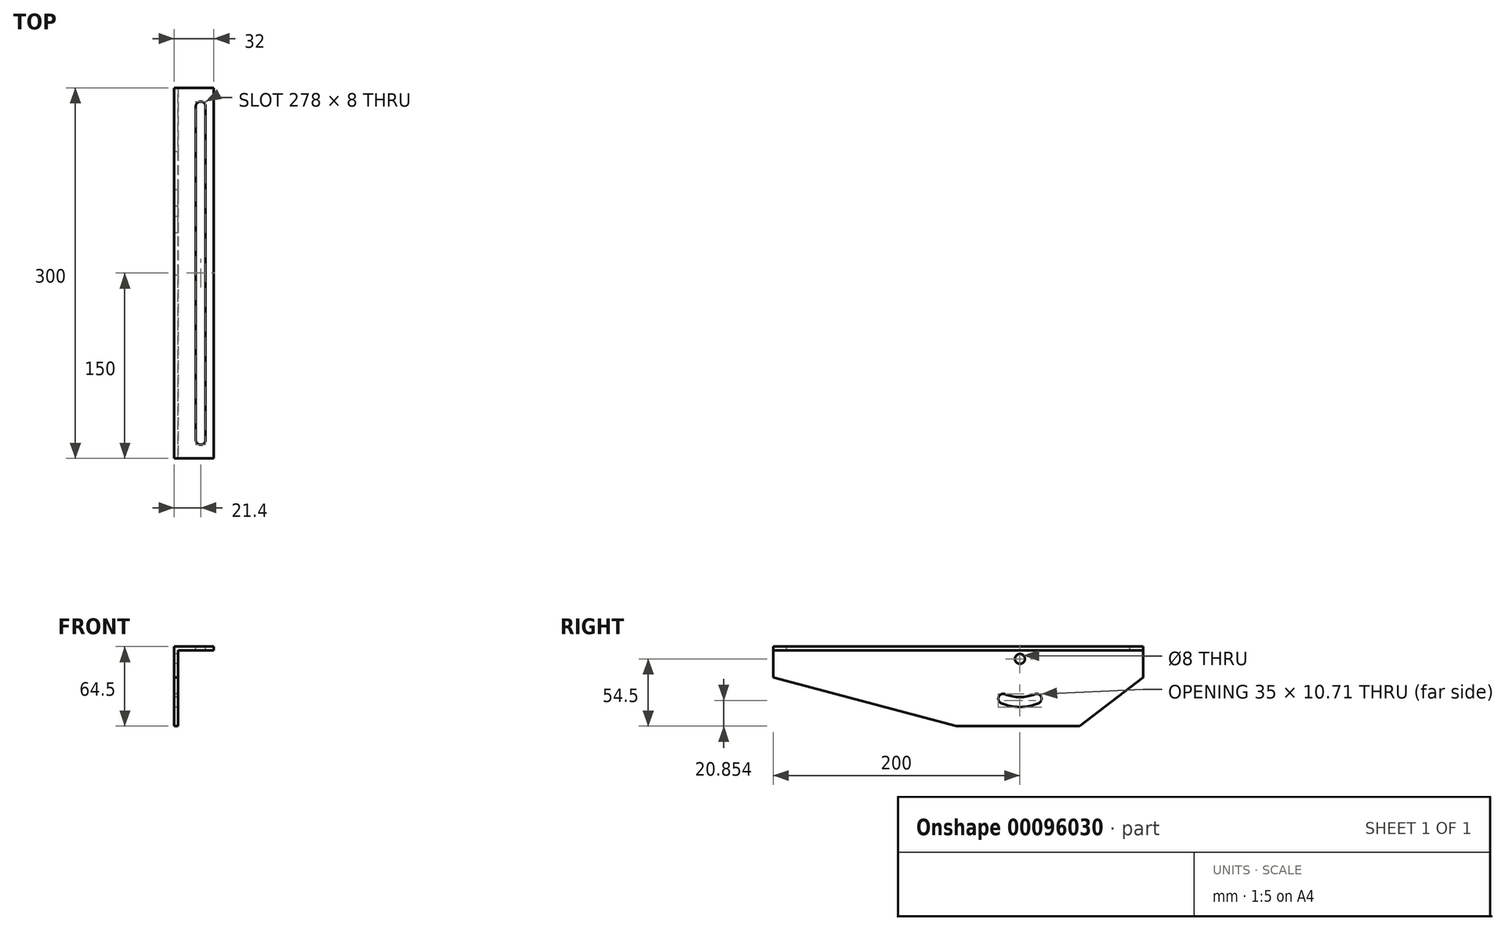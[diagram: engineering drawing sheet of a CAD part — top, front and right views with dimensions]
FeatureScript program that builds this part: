
annotation { "Feature Type Name" : "Feature", "Feature Type Description" : "" }
export const myFeature = defineFeature(function(context is Context, id is Id, definition is map)
    precondition{}
    {
        {
            var Q0;
            Q0=qCreatedBy(makeId("Right.planeOp"),FACE);
            var sketch = newSketch(context, id + "F0", { "sketchPlane" : qUnion([Q0])});
            skLineSegment(sketch, "E0", {"start": v(150, 0) * mm, "end": v(-150, 0) * mm});
            skLineSegment(sketch, "E1", {"start": v(-150, 0) * mm, "end": v(-150, -25) * mm});
            skLineSegment(sketch, "E2", {"start": v(150, 0) * mm, "end": v(150, -25) * mm});
            skLineSegment(sketch, "E3", {"start": v(150, -25) * mm, "end": v(98.38, -64.5) * mm});
            skLineSegment(sketch, "E4", {"start": v(98.38, -64.5) * mm, "end": v(-1.62, -64.5) * mm});
            skLineSegment(sketch, "E5", {"start": v(-1.62, -64.5) * mm, "end": v(-150, -25) * mm});
            skSolve(sketch);
        }
        {
            var Q0;
            Q0=makeQuery(id+"F0.imprint","IMPRINT",FACE,{"disambiguationData":[TD([[makeQuery(id+"F0.imprint","IMPRINT",EDGE,{"derivedFrom":sQuery(id+"F0.wireOp",EDGE,"E0")}),1.0]])]});
            extrude(context, id + "F1", {"entities" : qUnion([Q0]), "depth" : 3 * mm});
        }
        {
            var Q0;
            Q0=makeQuery(id+"F1.opExtrude","CAP_FACE",FACE,{"disambiguationData":[OSD([sQuery(id+"F0.wireOp",EDGE,"E0"),sQuery(id+"F0.wireOp",EDGE,"E1"),sQuery(id+"F0.wireOp",EDGE,"E2"),sQuery(id+"F0.wireOp",EDGE,"E3"),sQuery(id+"F0.wireOp",EDGE,"E4"),sQuery(id+"F0.wireOp",EDGE,"E5")])],"isStart":false});
            var sketch = newSketch(context, id + "F2", { "sketchPlane" : qUnion([Q0])});
            skLineSegment(sketch, "E6.bottom", {"start": v(-150, 0) * mm, "end": v(150, 0) * mm});
            skLineSegment(sketch, "E6.top", {"start": v(-150, -3) * mm, "end": v(150, -3) * mm});
            skLineSegment(sketch, "E6.left", {"start": v(-150, 0) * mm, "end": v(-150, -3) * mm});
            skLineSegment(sketch, "E6.right", {"start": v(150, 0) * mm, "end": v(150, -3) * mm});
            skSolve(sketch);
        }
        {
            var Q0;
            Q0 = qSketchRegion(id + "F2", true);
            extrude(context, id + "F3", {"entities" : qUnion([Q0]), "operationType" : NewBodyOperationType.ADD, "depth" : 29 * mm});
        }
        {
            var Q0;
            Q0=makeQuery(id+"F3.boolean.opBoolean","MERGE",FACE,{"derivedFrom":[makeQuery(id+"F1.opExtrude","SWEPT_FACE",FACE,{"disambiguationData":[OSD([sQuery(id+"F0.wireOp",EDGE,"E0")])]}),makeQuery(id+"F3.opExtrude","SWEPT_FACE",FACE,{"disambiguationData":[OSD([sQuery(id+"F2.wireOp",EDGE,"E6.bottom")])]})]});
            var sketch = newSketch(context, id + "F4", { "sketchPlane" : qUnion([Q0])});
            skLineSegment(sketch, "E7", {"start": v(21.4, -135) * mm, "end": v(21.4, 135) * mm});
            skArc(sketch, "E8.0.startCap", {"start": v(25.4, -135) * mm, "mid": v(21.4, -139) * mm, "end": v(17.4, -135) * mm});
            skArc(sketch, "E8.0.endCap", {"start": v(17.4, 135) * mm, "mid": v(21.4, 139) * mm, "end": v(25.4, 135) * mm});
            skLineSegment(sketch, "E8.0.left", {"start": v(17.4, -135) * mm, "end": v(17.4, 135) * mm});
            skLineSegment(sketch, "E8.0.right", {"start": v(25.4, -135) * mm, "end": v(25.4, 135) * mm});
            skSolve(sketch);
        }
        {
            var Q0;
            Q0 = qSketchRegion(id + "F4", true);
            extrude(context, id + "F5", {"entities" : qUnion([Q0]), "operationType" : NewBodyOperationType.REMOVE, "endBound" : BoundingType.THROUGH_ALL, "oppositeDirection" : true, "depth" : 25 * mm});
        }
        {
            var Q0;
            Q0=makeQuery(id+"F1.opExtrude","CAP_FACE",FACE,{"disambiguationData":[OSD([sQuery(id+"F0.wireOp",EDGE,"E0"),sQuery(id+"F0.wireOp",EDGE,"E1"),sQuery(id+"F0.wireOp",EDGE,"E2"),sQuery(id+"F0.wireOp",EDGE,"E3"),sQuery(id+"F0.wireOp",EDGE,"E4"),sQuery(id+"F0.wireOp",EDGE,"E5")])],"isStart":true});
            var sketch = newSketch(context, id + "F6", { "sketchPlane" : qUnion([Q0])});
            skCircle(sketch, "E9", {"center": v(-50, -10) * mm, "radius": 4 * mm});
            skArc(sketch, "E10", {"start": v(-63.5, -42.3) * mm, "mid": v(-50, -45) * mm, "end": v(-36.5, -42.3) * mm});
            skArc(sketch, "E11.0.startCap", {"start": v(-65.04, -45.98) * mm, "mid": v(-67.2, -40.75) * mm, "end": v(-61.96, -38.6) * mm});
            skArc(sketch, "E11.0.endCap", {"start": v(-38.04, -38.6) * mm, "mid": v(-32.8, -40.75) * mm, "end": v(-34.96, -45.98) * mm});
            skArc(sketch, "E11.0.left", {"start": v(-61.96, -38.6) * mm, "mid": v(-50, -41) * mm, "end": v(-38.04, -38.6) * mm});
            skArc(sketch, "E11.0.right", {"start": v(-65.04, -45.98) * mm, "mid": v(-50, -49) * mm, "end": v(-34.96, -45.98) * mm});
            skSolve(sketch);
        }
        {
            var Q0;
            Q0 = qSketchRegion(id + "F6", true);
            extrude(context, id + "F7", {"entities" : qUnion([Q0]), "operationType" : NewBodyOperationType.REMOVE, "endBound" : BoundingType.THROUGH_ALL, "oppositeDirection" : true, "depth" : 25 * mm});
        }
    });
